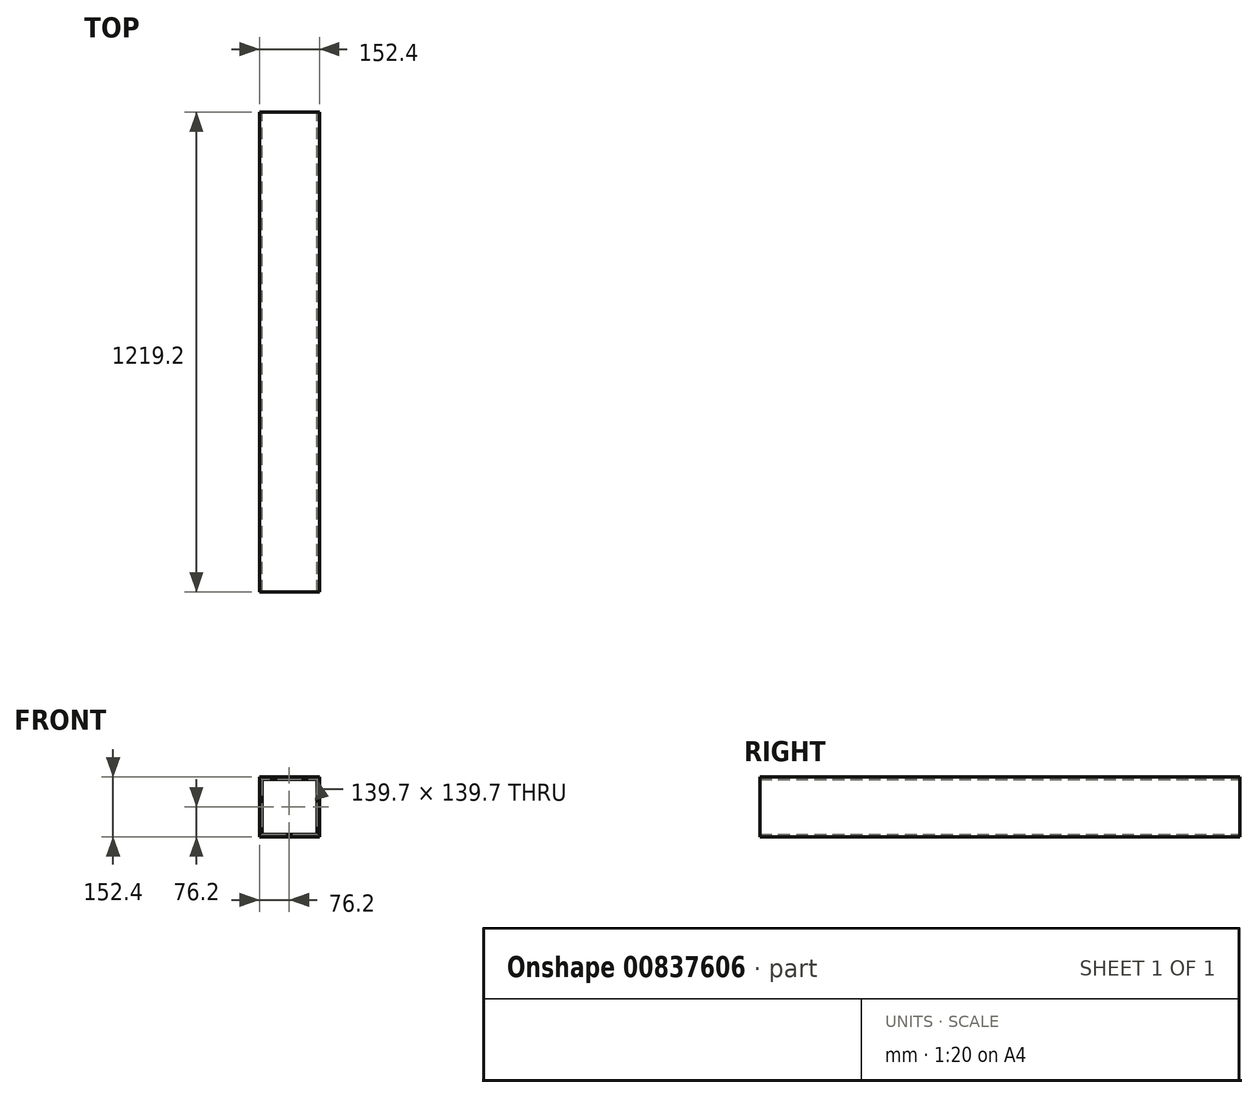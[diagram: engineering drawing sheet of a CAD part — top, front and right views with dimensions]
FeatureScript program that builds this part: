
annotation { "Feature Type Name" : "Feature", "Feature Type Description" : "" }
export const myFeature = defineFeature(function(context is Context, id is Id, definition is map)
    precondition{}
    {
        {
            var Q0;
            Q0=qCreatedBy(makeId("Front.planeOp"),FACE);
            var sketch = newSketch(context, id + "F0", { "sketchPlane" : qUnion([Q0])});
            skLineSegment(sketch, "E0.bottom", {"start": v(0, 0) * mm, "end": v(152.4, 0) * mm});
            skLineSegment(sketch, "E0.top", {"start": v(0, 152.4) * mm, "end": v(152.4, 152.4) * mm});
            skLineSegment(sketch, "E0.left", {"start": v(0, 0) * mm, "end": v(0, 152.4) * mm});
            skLineSegment(sketch, "E0.right", {"start": v(152.4, 0) * mm, "end": v(152.4, 152.4) * mm});
            skLineSegment(sketch, "E1.0", {"start": v(6.35, 146.05) * mm, "end": v(146.05, 146.05) * mm});
            skLineSegment(sketch, "E1.1", {"start": v(6.35, 6.35) * mm, "end": v(6.35, 146.05) * mm});
            skLineSegment(sketch, "E1.2", {"start": v(6.35, 6.35) * mm, "end": v(146.05, 6.35) * mm});
            skLineSegment(sketch, "E1.3", {"start": v(146.05, 6.35) * mm, "end": v(146.05, 146.05) * mm});
            skSolve(sketch);
        }
        {
            var Q0;
            Q0=makeQuery(id+"F0.imprint","IMPRINT",FACE,{"disambiguationData":[TD([[makeQuery(id+"F0.imprint","IMPRINT",EDGE,{"derivedFrom":sQuery(id+"F0.wireOp",EDGE,"E0.bottom")}),1.0]])]});
            extrude(context, id + "F1", {"entities" : qUnion([Q0]), "depth" : 1219.2 * mm, "offsetDistance" : 25.4 * mm});
        }
    });
